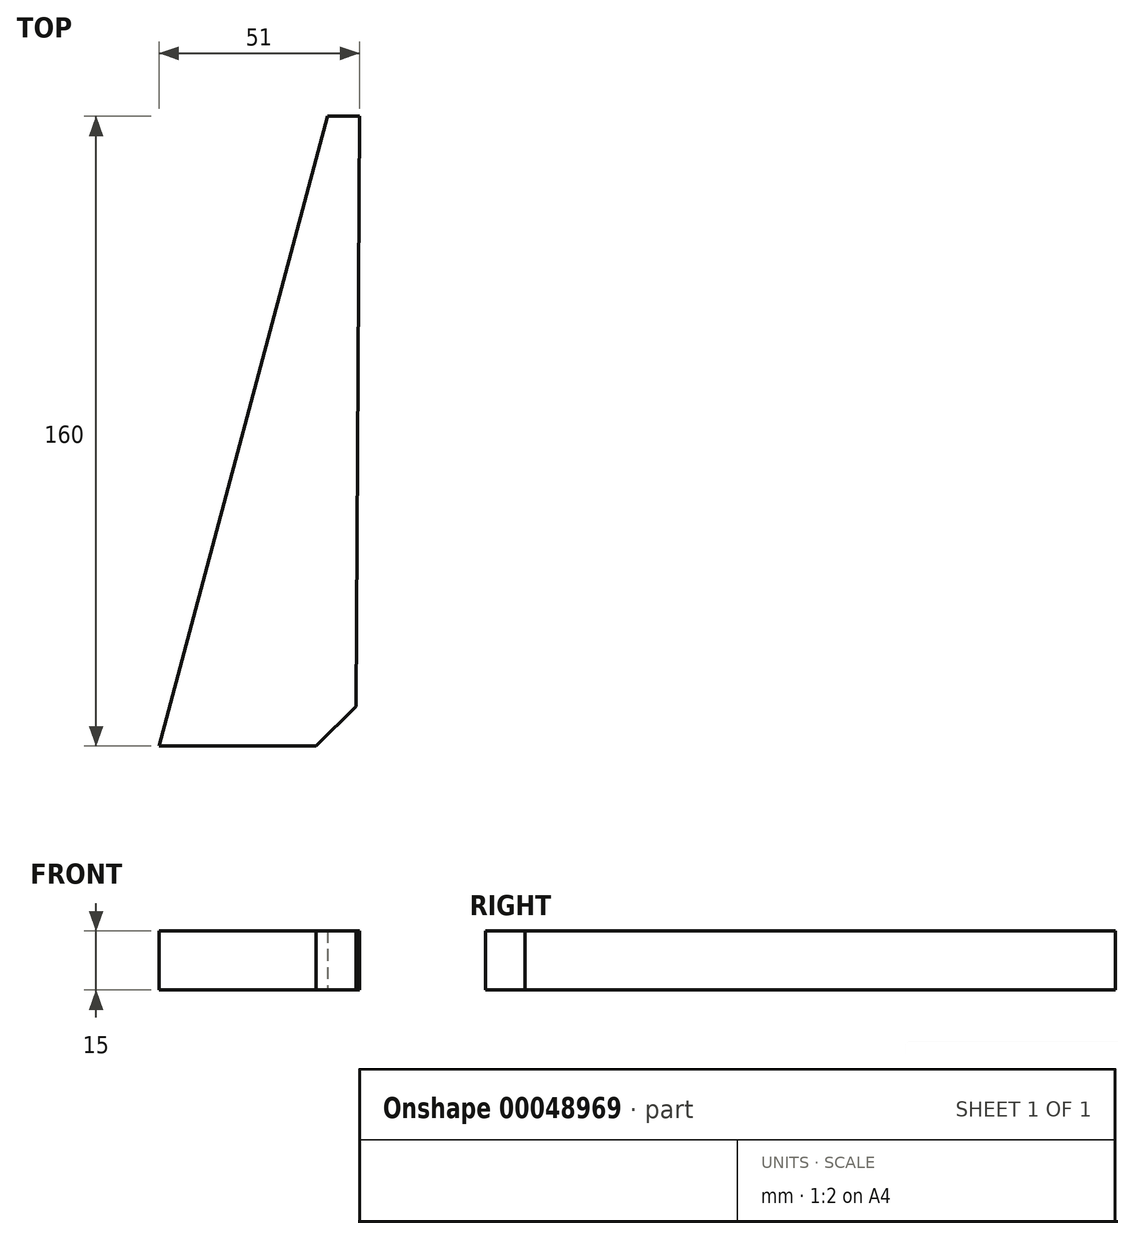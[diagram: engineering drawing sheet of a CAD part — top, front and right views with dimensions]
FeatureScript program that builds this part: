
annotation { "Feature Type Name" : "Feature", "Feature Type Description" : "" }
export const myFeature = defineFeature(function(context is Context, id is Id, definition is map)
    precondition{}
    {
        {
            var Q0;
            Q0=qCreatedBy(makeId("Top.planeOp"),FACE);
            var sketch = newSketch(context, id + "F0", { "sketchPlane" : qUnion([Q0])});
            skLineSegment(sketch, "E0", {"start": v(0, 0) * mm, "end": v(-50, 0) * mm});
            skLineSegment(sketch, "E1", {"start": v(1, 160) * mm, "end": v(0, 0) * mm});
            skLineSegment(sketch, "E2", {"start": v(-7.13, 160) * mm, "end": v(-50, 0) * mm});
            skLineSegment(sketch, "E3", {"start": v(-7.13, 160) * mm, "end": v(1, 160) * mm});
            skSolve(sketch);
        }
        {
            var Q0;
            Q0=makeQuery(id+"F0.imprint","IMPRINT",FACE,{"disambiguationData":[TD([[makeQuery(id+"F0.imprint","IMPRINT",EDGE,{"derivedFrom":sQuery(id+"F0.wireOp",EDGE,"E0")}),-1.0]])]});
            extrude(context, id + "F1", {"entities" : qUnion([Q0]), "depth" : 15 * mm});
        }
        {
            var Q0;
            Q0=makeQuery(id+"F1.opExtrude","SWEPT_EDGE",EDGE,{"disambiguationData":[OSD([sQuery(id+"F0.wireOp",EDGE,"E0"),sQuery(id+"F0.wireOp",EDGE,"E1")])]});
            chamfer(context, id + "F2", {"entities" : qUnion([Q0]), "chamferType" : ChamferType.OFFSET_ANGLE, "width" : 10 * mm, "oppositeDirection" : false, "angle" : 45 * degree, "tangentPropagation" : true});
        }
    });
